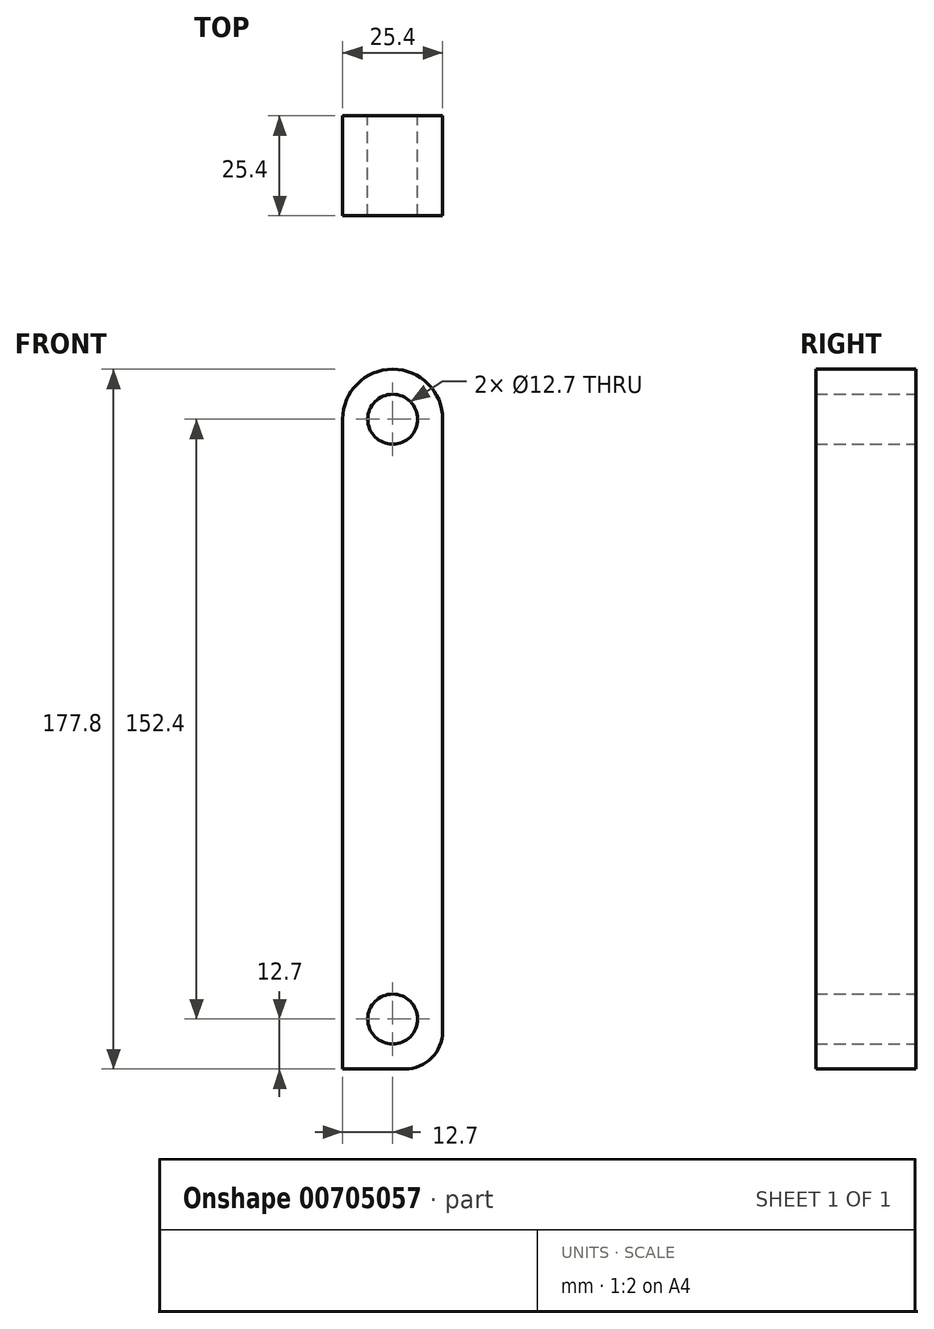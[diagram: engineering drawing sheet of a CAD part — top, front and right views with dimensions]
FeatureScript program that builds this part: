
annotation { "Feature Type Name" : "Feature", "Feature Type Description" : "" }
export const myFeature = defineFeature(function(context is Context, id is Id, definition is map)
    precondition{}
    {
        {
            var Q0;
            Q0=qCreatedBy(makeId("Front.planeOp"),FACE);
            var sketch = newSketch(context, id + "F0", { "sketchPlane" : qUnion([Q0])});
            skLineSegment(sketch, "E0", {"start": v(0, 0) * mm, "end": v(0, 177.8) * mm});
            skLineSegment(sketch, "E1", {"start": v(0, 177.8) * mm, "end": v(25.4, 177.8) * mm});
            skLineSegment(sketch, "E2", {"start": v(25.4, 177.8) * mm, "end": v(25.4, 9.58) * mm});
            skLineSegment(sketch, "E3", {"start": v(0, 0) * mm, "end": v(15.82, 0) * mm});
            skArc(sketch, "E4", {"start": v(15.82, 0) * mm, "mid": v(22.6, 2.8) * mm, "end": v(25.4, 9.58) * mm});
            skPoint(sketch, "E5", {"position": v(12.7, 177.8) * mm});
            skPoint(sketch, "E6", {"position": v(12.7, 165.1) * mm});
            skPoint(sketch, "E7", {"position": v(12.7, 12.7) * mm});
            skCircle(sketch, "E8", {"center": v(12.7, 165.1) * mm, "radius": 6.35 * mm});
            skCircle(sketch, "E9", {"center": v(12.7, 12.7) * mm, "radius": 6.35 * mm});
            skSolve(sketch);
        }
        {
            var Q0;
            Q0=makeQuery(id+"F0.imprint","IMPRINT",FACE,{"disambiguationData":[TD([[makeQuery(id+"F0.imprint","IMPRINT",EDGE,{"derivedFrom":sQuery(id+"F0.wireOp",EDGE,"E0")}),-1.0]])]});
            extrude(context, id + "F1", {"entities" : qUnion([Q0]), "depth" : 25.4 * mm, "offsetDistance" : 25.4 * mm});
        }
        {
            var Q0;
            Q0=makeQuery(id+"F1.opExtrude","SWEPT_EDGE",EDGE,{"disambiguationData":[OSD([sQuery(id+"F0.wireOp",EDGE,"E1"),sQuery(id+"F0.wireOp",EDGE,"E2")])]});
            fillet(context, id + "F2", {"entities" : qUnion([Q0]), "radius" : 12.7 * mm, "tangentPropagation" : true, "allowEdgeOverflow" : false});
        }
        {
            var Q0;
            Q0=makeQuery(id+"F1.opExtrude","SWEPT_EDGE",EDGE,{"disambiguationData":[OSD([sQuery(id+"F0.wireOp",EDGE,"E0"),sQuery(id+"F0.wireOp",EDGE,"E1")])]});
            fillet(context, id + "F3", {"entities" : qUnion([Q0]), "radius" : 12.7 * mm, "tangentPropagation" : true, "allowEdgeOverflow" : false});
        }
    });
